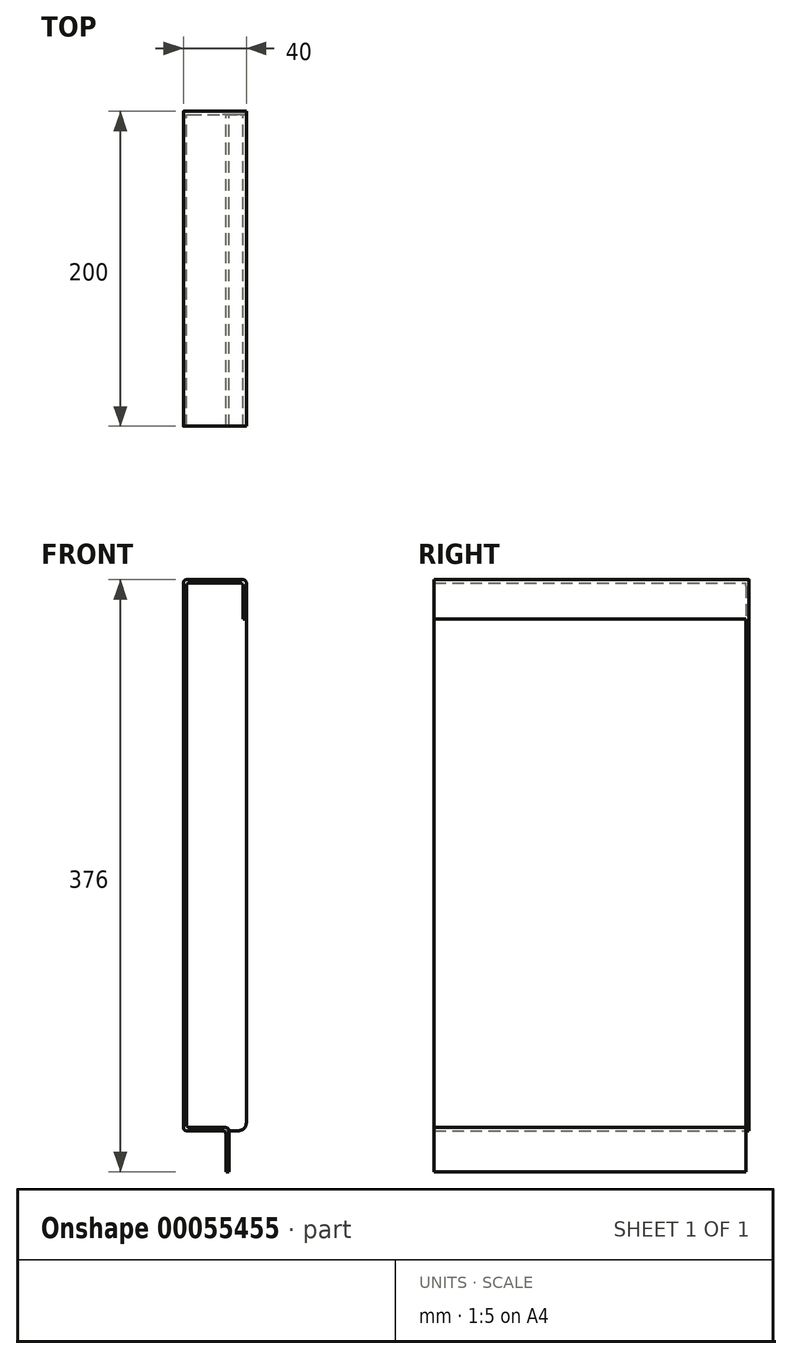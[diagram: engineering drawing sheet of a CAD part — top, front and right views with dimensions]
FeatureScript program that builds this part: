
annotation { "Feature Type Name" : "Feature", "Feature Type Description" : "" }
export const myFeature = defineFeature(function(context is Context, id is Id, definition is map)
    precondition{}
    {
        {
            var Q0;
            Q0=qCreatedBy(makeId("Front.planeOp"),FACE);
            var sketch = newSketch(context, id + "F0", { "sketchPlane" : qUnion([Q0])});
            skLineSegment(sketch, "E0", {"start": v(0, 0) * mm, "end": v(0, -350) * mm});
            skLineSegment(sketch, "E1", {"start": v(0, -350) * mm, "end": v(27, -350) * mm});
            skLineSegment(sketch, "E2", {"start": v(27, -350) * mm, "end": v(27, -376) * mm});
            skLineSegment(sketch, "E3", {"start": v(0, 0) * mm, "end": v(40, 0) * mm});
            skLineSegment(sketch, "E4", {"start": v(40, 0) * mm, "end": v(40, -25) * mm});
            skLineSegment(sketch, "E5.0", {"start": v(38, -2) * mm, "end": v(38, -25) * mm});
            skLineSegment(sketch, "E5.1", {"start": v(29, -348) * mm, "end": v(29, -376) * mm});
            skLineSegment(sketch, "E5.2", {"start": v(2, -348) * mm, "end": v(29, -348) * mm});
            skLineSegment(sketch, "E5.3", {"start": v(2, -2) * mm, "end": v(2, -348) * mm});
            skLineSegment(sketch, "E5.4", {"start": v(2, -2) * mm, "end": v(38, -2) * mm});
            skLineSegment(sketch, "E6", {"start": v(38, -25) * mm, "end": v(40, -25) * mm});
            skLineSegment(sketch, "E7", {"start": v(27, -376) * mm, "end": v(29, -376) * mm});
            skSolve(sketch);
        }
        {
            var Q0;
            Q0=qCreatedBy(makeId("Top.planeOp"),FACE);
            var sketch = newSketch(context, id + "F1", { "sketchPlane" : qUnion([Q0])});
            skLineSegment(sketch, "E8", {"start": v(0, 0) * mm, "end": v(0, 198) * mm});
            skSolve(sketch);
        }
        {
            var Q0;
            Q0=qSketchRegion(id+"F0",true);
            var Q1;
            Q1=qConstructionFilter(qBodyType(qCreatedBy(id+"F1",EDGE),BodyType.WIRE),ConstructionObject.NO);
            sweep(context, id + "F2", {"profiles" : qUnion([Q0]), "path" : qUnion([Q1])});
        }
        {
            var Q0;
            Q0=makeQuery(id+"F2.opSweep","CAP_FACE",FACE,{"disambiguationData":[OSD([sQuery(id+"F0.wireOp",EDGE,"E0"),sQuery(id+"F0.wireOp",EDGE,"E1"),sQuery(id+"F0.wireOp",EDGE,"E2"),sQuery(id+"F0.wireOp",EDGE,"E3"),sQuery(id+"F0.wireOp",EDGE,"E4"),sQuery(id+"F0.wireOp",EDGE,"E5.0"),sQuery(id+"F0.wireOp",EDGE,"E5.1"),sQuery(id+"F0.wireOp",EDGE,"E5.2"),sQuery(id+"F0.wireOp",EDGE,"E5.3"),sQuery(id+"F0.wireOp",EDGE,"E5.4"),sQuery(id+"F0.wireOp",EDGE,"E6"),sQuery(id+"F0.wireOp",EDGE,"E7"),sQuery(id+"F1.wireOp",VERTEX,"E8.end")])],"isStart":false});
            var sketch = newSketch(context, id + "F3", { "sketchPlane" : qUnion([Q0])});
            skLineSegment(sketch, "E9.0", {"start": v(0, -350) * mm, "end": v(0, 0) * mm});
            skLineSegment(sketch, "E10.0", {"start": v(-40, 0) * mm, "end": v(0, 0) * mm});
            skLineSegment(sketch, "E11.0", {"start": v(-40, -25) * mm, "end": v(-40, 0) * mm});
            skLineSegment(sketch, "E12.0", {"start": v(-40, -25) * mm, "end": v(-40, -345) * mm});
            skArc(sketch, "E13.0", {"start": v(-35, -350) * mm, "mid": v(-38.54, -348.54) * mm, "end": v(-40, -345) * mm});
            skLineSegment(sketch, "E14.0", {"start": v(-35, -350) * mm, "end": v(-29, -350) * mm});
            skLineSegment(sketch, "E15.0", {"start": v(-27, -350) * mm, "end": v(0, -350) * mm});
            skLineSegment(sketch, "E16", {"start": v(-29, -350) * mm, "end": v(-27, -350) * mm});
            skSolve(sketch);
        }
        {
            var Q0;
            Q0=qSketchRegion(id+"F3",true);
            extrude(context, id + "F4", {"entities" : qUnion([Q0]), "operationType" : NewBodyOperationType.ADD, "depth" : 2 * mm});
        }
        {
            var Q0;
            Q0=makeQuery(id+"F4.boolean.opBoolean","MERGE",EDGE,{"derivedFrom":[makeQuery(id+"F2.opSweep","SWEPT_EDGE",EDGE,{"disambiguationData":[OSD([sQuery(id+"F0.wireOp",EDGE,"E0"),sQuery(id+"F0.wireOp",EDGE,"E3"),sQuery(id+"F1.wireOp",EDGE,"E8")])]}),makeQuery(id+"F4.opExtrude","SWEPT_EDGE",EDGE,{"disambiguationData":[OSD([sQuery(id+"F3.wireOp",EDGE,"E9.0"),sQuery(id+"F3.wireOp",EDGE,"E10.0")])]})]});
            var Q1;
            Q1=makeQuery(id+"F4.boolean.opBoolean","MERGE",EDGE,{"derivedFrom":[makeQuery(id+"F2.opSweep","SWEPT_EDGE",EDGE,{"disambiguationData":[OSD([sQuery(id+"F0.wireOp",EDGE,"E3"),sQuery(id+"F0.wireOp",EDGE,"E4"),sQuery(id+"F1.wireOp",EDGE,"E8")])]}),makeQuery(id+"F4.opExtrude","SWEPT_EDGE",EDGE,{"disambiguationData":[OSD([sQuery(id+"F3.wireOp",EDGE,"E10.0"),sQuery(id+"F3.wireOp",EDGE,"E11.0")])]})]});
            var Q2;
            Q2=makeQuery(id+"F2.opSweep","SWEPT_EDGE",EDGE,{"disambiguationData":[OSD([sQuery(id+"F0.wireOp",EDGE,"E5.2"),sQuery(id+"F0.wireOp",EDGE,"E5.3"),sQuery(id+"F1.wireOp",EDGE,"E8")])]});
            var Q3;
            Q3=makeQuery(id+"F2.opSweep","SWEPT_EDGE",EDGE,{"disambiguationData":[OSD([sQuery(id+"F0.wireOp",EDGE,"E5.1"),sQuery(id+"F0.wireOp",EDGE,"E5.2"),sQuery(id+"F1.wireOp",EDGE,"E8")])]});
            var Q4;
            Q4=makeQuery(id+"F2.opSweep","SWEPT_EDGE",EDGE,{"disambiguationData":[OSD([sQuery(id+"F0.wireOp",EDGE,"E5.0"),sQuery(id+"F0.wireOp",EDGE,"E5.4"),sQuery(id+"F1.wireOp",EDGE,"E8")])]});
            var Q5;
            Q5=makeQuery(id+"F2.opSweep","SWEPT_EDGE",EDGE,{"disambiguationData":[OSD([sQuery(id+"F0.wireOp",EDGE,"E1"),sQuery(id+"F0.wireOp",EDGE,"E2"),sQuery(id+"F1.wireOp",EDGE,"E8")])]});
            var Q6;
            Q6=makeQuery(id+"F4.boolean.opBoolean","MERGE",EDGE,{"derivedFrom":[makeQuery(id+"F2.opSweep","SWEPT_EDGE",EDGE,{"disambiguationData":[OSD([sQuery(id+"F0.wireOp",EDGE,"E0"),sQuery(id+"F0.wireOp",EDGE,"E1"),sQuery(id+"F1.wireOp",EDGE,"E8")])]}),makeQuery(id+"F4.opExtrude","SWEPT_EDGE",EDGE,{"disambiguationData":[OSD([sQuery(id+"F3.wireOp",EDGE,"E9.0"),sQuery(id+"F3.wireOp",EDGE,"E15.0")])]})]});
            var Q7;
            Q7=makeQuery(id+"F2.opSweep","SWEPT_EDGE",EDGE,{"disambiguationData":[OSD([sQuery(id+"F0.wireOp",EDGE,"E5.3"),sQuery(id+"F0.wireOp",EDGE,"E5.4"),sQuery(id+"F1.wireOp",EDGE,"E8")])]});
            fillet(context, id + "F5", {"entities" : qUnion([Q0, Q1, Q2, Q3, Q4, Q5, Q6, Q7]), "radius" : 2 * mm, "tangentPropagation" : true, "allowEdgeOverflow" : false});
        }
    });
